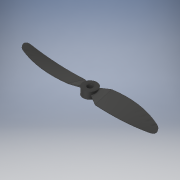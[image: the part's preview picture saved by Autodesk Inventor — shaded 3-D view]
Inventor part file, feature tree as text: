
AUTODESK INVENTOR PART (.ipt)
format: ipt  version: 2019.4 (Build 234330000, 330)  size: 423,936 bytes
history: native  units: mm
features: sketch x13, plane x6, other x6, loft x3, projected_geometry x3, extrude x2, fillet x2, sweep x2, pattern_circular x1, thread x1, delete_face x1
ambient origin geometry x8: Origin, YZ Plane, XZ Plane, XY Plane, X Axis, Y Axis, Z Axis, Center Point
bodies: Solid1 (feature_tree)
feature tree (40):
  extrude  "Extrusion1"  Depth=12.25mm
  plane  "Work Plane1"
  other  "Base Loft Sketch"
  sketch  "Sketch3"  dims[d2=6.0mm d3=0.0mm d4=5.5mm]
  plane  "Work Plane2"
  other  "Second Loft Sketch"
  sketch  "Sketch5"  dims[d5=4.0mm d6=1.0mm]
  plane  "Work Plane3"
  sketch  "Sketch6"  dims[d8=8.8mm d9=5.75mm d11=14.75mm d12=0.4mm]
  sketch  "Sketch7"  dims[d13=25.0mm d14=14.75mm]
  plane  "Work Plane4"
  other  "4th Loft Sketch"
  sketch  "Sketch9"  dims[d15=23.9mm d16=3.0mm]
  plane  "Work Plane5"
  other  "Final Loft Sketch"
  loft  "Loft1"
  loft  "Loft2"
  loft  "Loft3"
  fillet  "Fillet1"  Radius=14.75mm
  fillet  "Fillet2"  Radius=0.4mm
  sketch  "Sketch13"  dims[d18=7.25mm]
  plane  "Work Plane7"
  sweep  "Sweep1"
  sweep  "Sweep2"
  pattern_circular  "Circular Pattern1"  [2 undecoded]
  thread  "Thread1"  [1 undecoded]
  extrude  "Extrusion3"  TaperAngle=0.0deg  [1 undecoded]
  delete_face  "Delete Face1"
  sketch  "Sketch1"  dims[d0=5.0mm d1=12.25mm]
  projected_geometry  "Projected Loop1"
  other  "Edges1"
  other  "Edges2"
  sketch  "Sketch14"  dims[d19=0.4mm]
  projected_geometry  "Projected Loop6"
  sketch  "Sketch15"  dims[d20=0.872665mm]
  sketch  "Sketch16"  dims[d21=2.5mm]
  sketch  "Sketch17"  dims[d22=0.4mm]
  sketch  "Sketch18"  dims[d23=2.5mm]
  sketch  "Sketch19"  dims[d24=0.75mm d25=3.2mm d26=0.436332mm d27=0.0mm d28=90.0deg d29=0.0mm d30=90.0deg d31=0.0mm d32=90.0deg d33=0.0mm d34=90.0deg d35=0.0mm d36=90.0deg d43=0.0mm d44=90.0deg d45=0.0mm d46=90.0deg d47=9.0mm d48=2.0mm d51=10.0mm d52=0.0mm d53=0.0mm d54=0.0mm d55=0.0mm d56=0.0mm d57=20.0mm d58=360.0deg d60=10.0mm d61=0.0mm]
  projected_geometry  "Project Cut Edges1"
note: 4 required parameter values undecoded (feature->parameter linkage not recoverable at this tier; creation-order binding heuristic only, values carry confidence <= 0.55)
